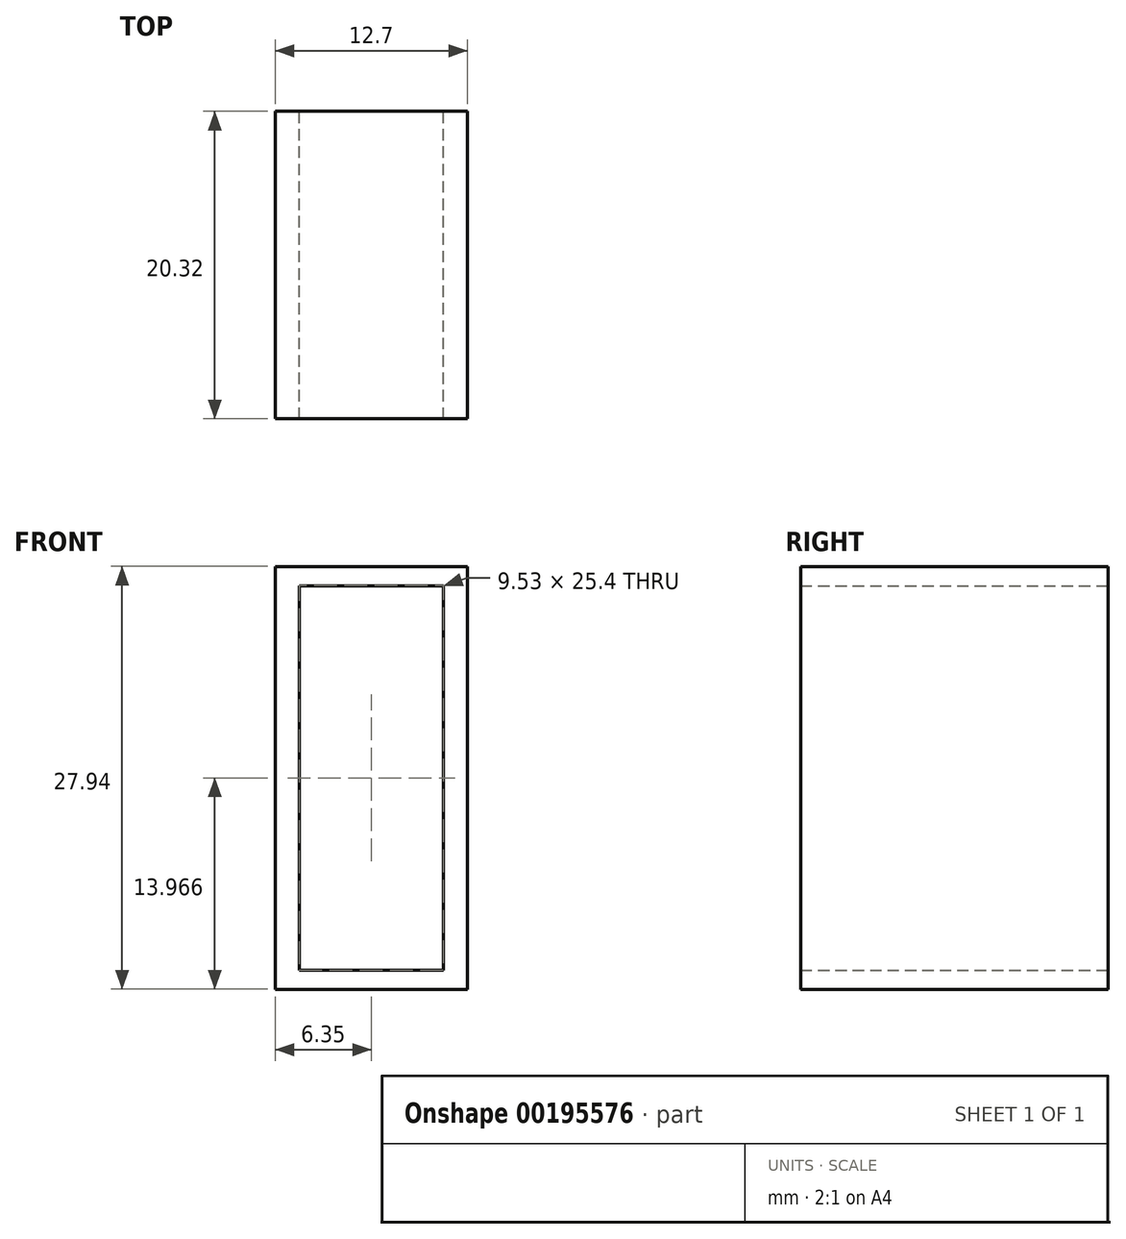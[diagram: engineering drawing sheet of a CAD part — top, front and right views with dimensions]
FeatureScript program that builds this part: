
annotation { "Feature Type Name" : "Feature", "Feature Type Description" : "" }
export const myFeature = defineFeature(function(context is Context, id is Id, definition is map)
    precondition{}
    {
        {
            var Q0;
            Q0=qCreatedBy(makeId("Front.planeOp"),FACE);
            var sketch = newSketch(context, id + "F0", { "sketchPlane" : qUnion([Q0])});
            skLineSegment(sketch, "E0.bottom", {"start": v(4.76, -10.72) * mm, "end": v(-4.76, -10.72) * mm});
            skLineSegment(sketch, "E0.top", {"start": v(4.76, 14.68) * mm, "end": v(-4.76, 14.68) * mm});
            skLineSegment(sketch, "E0.left", {"start": v(4.76, -10.72) * mm, "end": v(4.76, 14.68) * mm});
            skLineSegment(sketch, "E0.right", {"start": v(-4.76, -10.72) * mm, "end": v(-4.76, 14.68) * mm});
            skPoint(sketch, "E0.middle", {"position": v(0, 1.98) * mm});
            skLineSegment(sketch, "E1.bottom", {"start": v(6.35, -12) * mm, "end": v(-6.35, -12) * mm});
            skLineSegment(sketch, "E1.top", {"start": v(6.35, 15.95) * mm, "end": v(-6.35, 15.95) * mm});
            skLineSegment(sketch, "E1.left", {"start": v(6.35, -12) * mm, "end": v(6.35, 15.95) * mm});
            skLineSegment(sketch, "E1.right", {"start": v(-6.35, -12) * mm, "end": v(-6.35, 15.95) * mm});
            skSolve(sketch);
        }
        {
            var Q0;
            Q0 = qSketchRegion(id + "F0", true);
            extrude(context, id + "F1", {"entities" : qUnion([Q0]), "depth" : 20.32 * mm});
        }
    });
